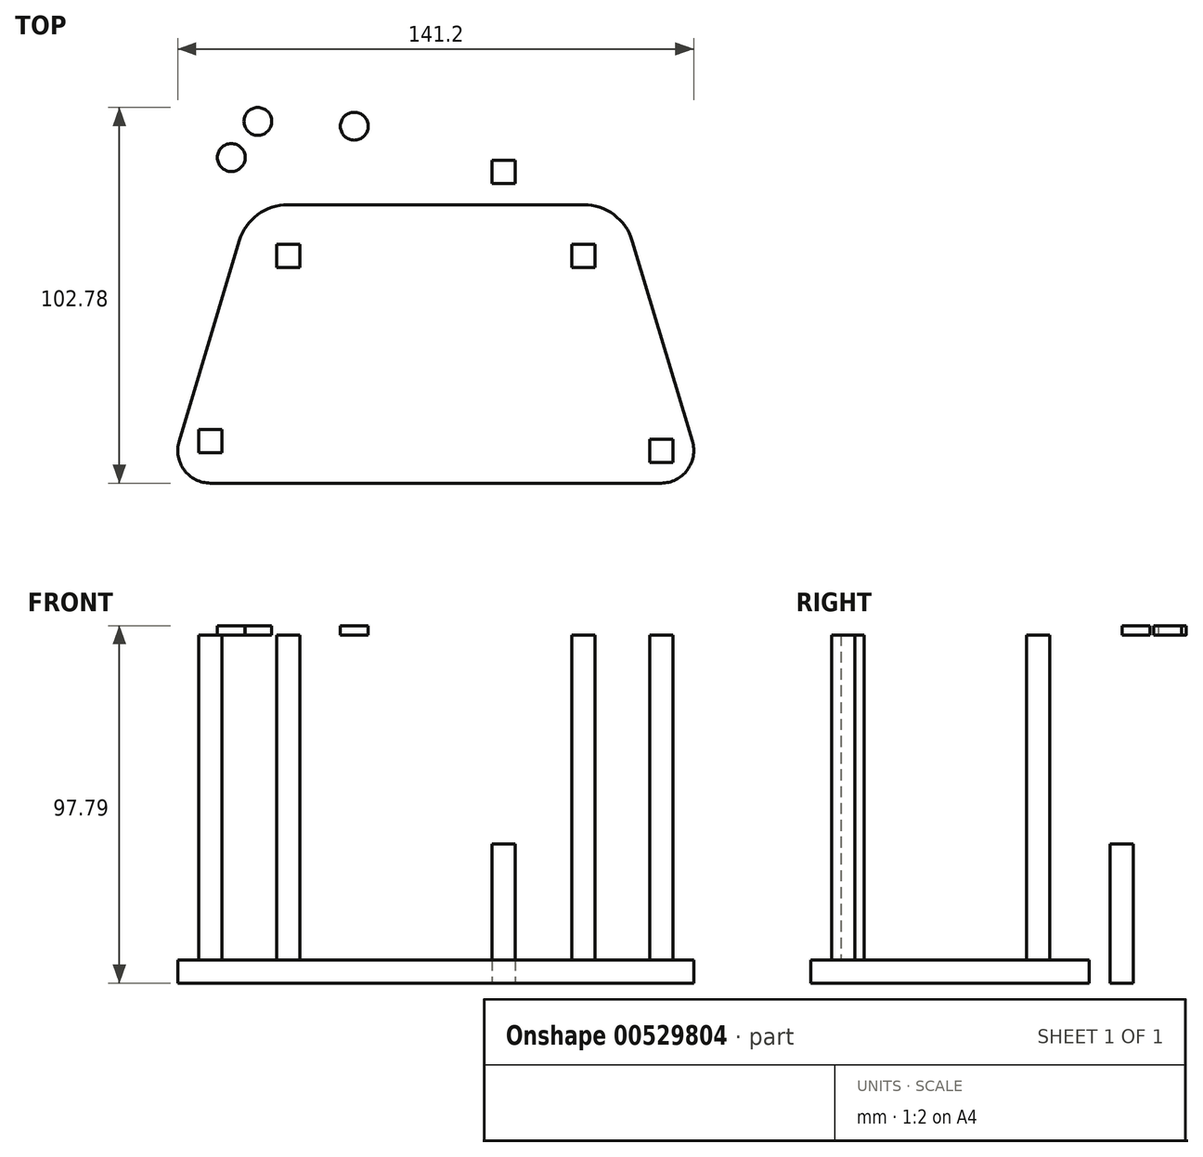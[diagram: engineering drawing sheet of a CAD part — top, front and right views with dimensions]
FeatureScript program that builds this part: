
annotation { "Feature Type Name" : "Feature", "Feature Type Description" : "" }
export const myFeature = defineFeature(function(context is Context, id is Id, definition is map)
    precondition{}
    {
        {
            var Q0;
            Q0=qCreatedBy(makeId("Top.planeOp"),FACE);
            var sketch = newSketch(context, id + "F0", { "sketchPlane" : qUnion([Q0])});
            skLineSegment(sketch, "E0.bottom", {"start": v(-40.4, 38.1) * mm, "end": v(40.4, 38.1) * mm});
            skLineSegment(sketch, "E0.top", {"start": v(-50.8, -38.1) * mm, "end": v(50.8, -38.1) * mm});
            skLineSegment(sketch, "E0.left", {"start": v(-50.8, 38.1) * mm, "end": v(-50.8, -38.1) * mm});
            skLineSegment(sketch, "E0.right", {"start": v(50.8, 38.1) * mm, "end": v(50.8, -38.1) * mm});
            skPoint(sketch, "E0.middle", {"position": v(0, 0) * mm});
            skLineSegment(sketch, "E1", {"start": v(-50.8, -38.1) * mm, "end": v(-61.71, -38.1) * mm});
            skLineSegment(sketch, "E2", {"start": v(-70.23, -26.66) * mm, "end": v(-53.79, 28.14) * mm});
            skLineSegment(sketch, "E3", {"start": v(50.8, -38.1) * mm, "end": v(61.71, -38.1) * mm});
            skLineSegment(sketch, "E4", {"start": v(70.23, -26.66) * mm, "end": v(53.79, 28.14) * mm});
            skPoint(sketch, "E5.visualSharp", {"position": v(-50.8, 38.1) * mm});
            skArc(sketch, "E5.filletArc", {"start": v(-40.4, 38.1) * mm, "mid": v(-48.75, 35.34) * mm, "end": v(-53.79, 28.14) * mm});
            skPoint(sketch, "E6.visualSharp", {"position": v(50.8, 38.1) * mm});
            skArc(sketch, "E6.filletArc", {"start": v(53.79, 28.14) * mm, "mid": v(48.75, 35.34) * mm, "end": v(40.4, 38.1) * mm});
            skPoint(sketch, "E7.visualSharp", {"position": v(73.66, -38.1) * mm});
            skArc(sketch, "E7.filletArc", {"start": v(61.71, -38.1) * mm, "mid": v(68.84, -34.52) * mm, "end": v(70.23, -26.66) * mm});
            skPoint(sketch, "E8.visualSharp", {"position": v(-73.66, -38.1) * mm});
            skArc(sketch, "E8.filletArc", {"start": v(-70.23, -26.66) * mm, "mid": v(-68.84, -34.52) * mm, "end": v(-61.71, -38.1) * mm});
            skSolve(sketch);
        }
        {
            var Q0;
            Q0 = qSketchRegion(id + "F0", true);
            extrude(context, id + "F1", {"entities" : qUnion([Q0]), "depth" : 6.35 * mm, "offsetDistance" : 25.4 * mm});
        }
        {
            var Q0;
            Q0=makeQuery(id+"F1.opExtrude","CAP_FACE",FACE,{"disambiguationData":[OSD([sQuery(id+"F0.wireOp",EDGE,"E0.bottom"),sQuery(id+"F0.wireOp",EDGE,"E0.top"),sQuery(id+"F0.wireOp",EDGE,"E1"),sQuery(id+"F0.wireOp",EDGE,"E2"),sQuery(id+"F0.wireOp",EDGE,"E3"),sQuery(id+"F0.wireOp",EDGE,"E4"),sQuery(id+"F0.wireOp",EDGE,"E5.filletArc"),sQuery(id+"F0.wireOp",EDGE,"E6.filletArc"),sQuery(id+"F0.wireOp",EDGE,"E7.filletArc"),sQuery(id+"F0.wireOp",EDGE,"E8.filletArc")])],"isStart":false});
            var sketch = newSketch(context, id + "F2", { "sketchPlane" : qUnion([Q0])});
            skLineSegment(sketch, "E9.bottom", {"start": v(-43.58, 27.3) * mm, "end": v(-37.23, 27.3) * mm});
            skLineSegment(sketch, "E9.top", {"start": v(-43.58, 20.95) * mm, "end": v(-37.23, 20.95) * mm});
            skLineSegment(sketch, "E9.left", {"start": v(-43.58, 27.3) * mm, "end": v(-43.58, 20.95) * mm});
            skLineSegment(sketch, "E9.right", {"start": v(-37.23, 27.3) * mm, "end": v(-37.23, 20.95) * mm});
            skPoint(sketch, "E9.middle", {"position": v(-40.4, 24.13) * mm});
            skLineSegment(sketch, "E10.bottom", {"start": v(37.23, 27.3) * mm, "end": v(43.58, 27.3) * mm});
            skLineSegment(sketch, "E10.top", {"start": v(37.23, 20.96) * mm, "end": v(43.58, 20.96) * mm});
            skLineSegment(sketch, "E10.left", {"start": v(37.23, 27.3) * mm, "end": v(37.23, 20.95) * mm});
            skLineSegment(sketch, "E10.right", {"start": v(43.58, 27.3) * mm, "end": v(43.58, 20.95) * mm});
            skPoint(sketch, "E10.middle", {"position": v(40.4, 24.13) * mm});
            skLineSegment(sketch, "E11.bottom", {"start": v(-64.89, -29.83) * mm, "end": v(-58.54, -29.83) * mm});
            skLineSegment(sketch, "E11.top", {"start": v(-64.89, -23.48) * mm, "end": v(-58.54, -23.48) * mm});
            skLineSegment(sketch, "E11.left", {"start": v(-64.89, -29.83) * mm, "end": v(-64.89, -23.48) * mm});
            skLineSegment(sketch, "E11.right", {"start": v(-58.54, -29.83) * mm, "end": v(-58.54, -23.48) * mm});
            skPoint(sketch, "E11.middle", {"position": v(-61.71, -26.66) * mm});
            skLineSegment(sketch, "E12.bottom", {"start": v(58.54, -26.03) * mm, "end": v(64.89, -26.03) * mm});
            skLineSegment(sketch, "E12.top", {"start": v(58.54, -32.38) * mm, "end": v(64.89, -32.38) * mm});
            skLineSegment(sketch, "E12.left", {"start": v(58.54, -26.03) * mm, "end": v(58.54, -32.38) * mm});
            skLineSegment(sketch, "E12.right", {"start": v(64.89, -26.03) * mm, "end": v(64.89, -32.38) * mm});
            skPoint(sketch, "E12.middle", {"position": v(61.71, -29.2) * mm});
            skSolve(sketch);
        }
        {
            var Q0;
            Q0 = qSketchRegion(id + "F2", true);
            extrude(context, id + "F3", {"entities" : qUnion([Q0]), "operationType" : NewBodyOperationType.ADD, "depth" : 88.9 * mm, "offsetDistance" : 25.4 * mm});
        }
        {
            var Q0;
            Q0=makeQuery(id+"F3.opExtrude","CAP_FACE",FACE,{"disambiguationData":[OSD([sQuery(id+"F2.wireOp",EDGE,"E11.bottom"),sQuery(id+"F2.wireOp",EDGE,"E11.top"),sQuery(id+"F2.wireOp",EDGE,"E11.left"),sQuery(id+"F2.wireOp",EDGE,"E11.right")])],"isStart":false});
            var sketch = newSketch(context, id + "F4", { "sketchPlane" : qUnion([Q0])});
            skCircle(sketch, "E13", {"center": v(-48.7, 60.87) * mm, "radius": 3.81 * mm});
            skCircle(sketch, "E14", {"center": v(-55.95, 50.98) * mm, "radius": 3.81 * mm});
            skCircle(sketch, "E15", {"center": v(-22.3, 59.55) * mm, "radius": 3.81 * mm});
            skSolve(sketch);
        }
        {
            var Q0;
            Q0 = qSketchRegion(id + "F4", true);
            extrude(context, id + "F5", {"entities" : qUnion([Q0]), "depth" : 2.54 * mm, "offsetDistance" : 25.4 * mm});
        }
        {
            var Q0;
            Q0=qCreatedBy(makeId("Top.planeOp"),FACE);
            var sketch = newSketch(context, id + "F6", { "sketchPlane" : qUnion([Q0])});
            skLineSegment(sketch, "E16.bottom", {"start": v(21.79, 50.23) * mm, "end": v(15.44, 50.23) * mm});
            skLineSegment(sketch, "E16.top", {"start": v(21.79, 43.88) * mm, "end": v(15.44, 43.88) * mm});
            skLineSegment(sketch, "E16.left", {"start": v(21.79, 50.23) * mm, "end": v(21.79, 43.88) * mm});
            skLineSegment(sketch, "E16.right", {"start": v(15.44, 50.23) * mm, "end": v(15.44, 43.88) * mm});
            skPoint(sketch, "E16.middle", {"position": v(18.61, 47.05) * mm});
            skSolve(sketch);
        }
        {
            var Q0;
            Q0 = qSketchRegion(id + "F6", true);
            extrude(context, id + "F7", {"entities" : qUnion([Q0]), "depth" : 38.1 * mm, "offsetDistance" : 25.4 * mm});
        }
    });
